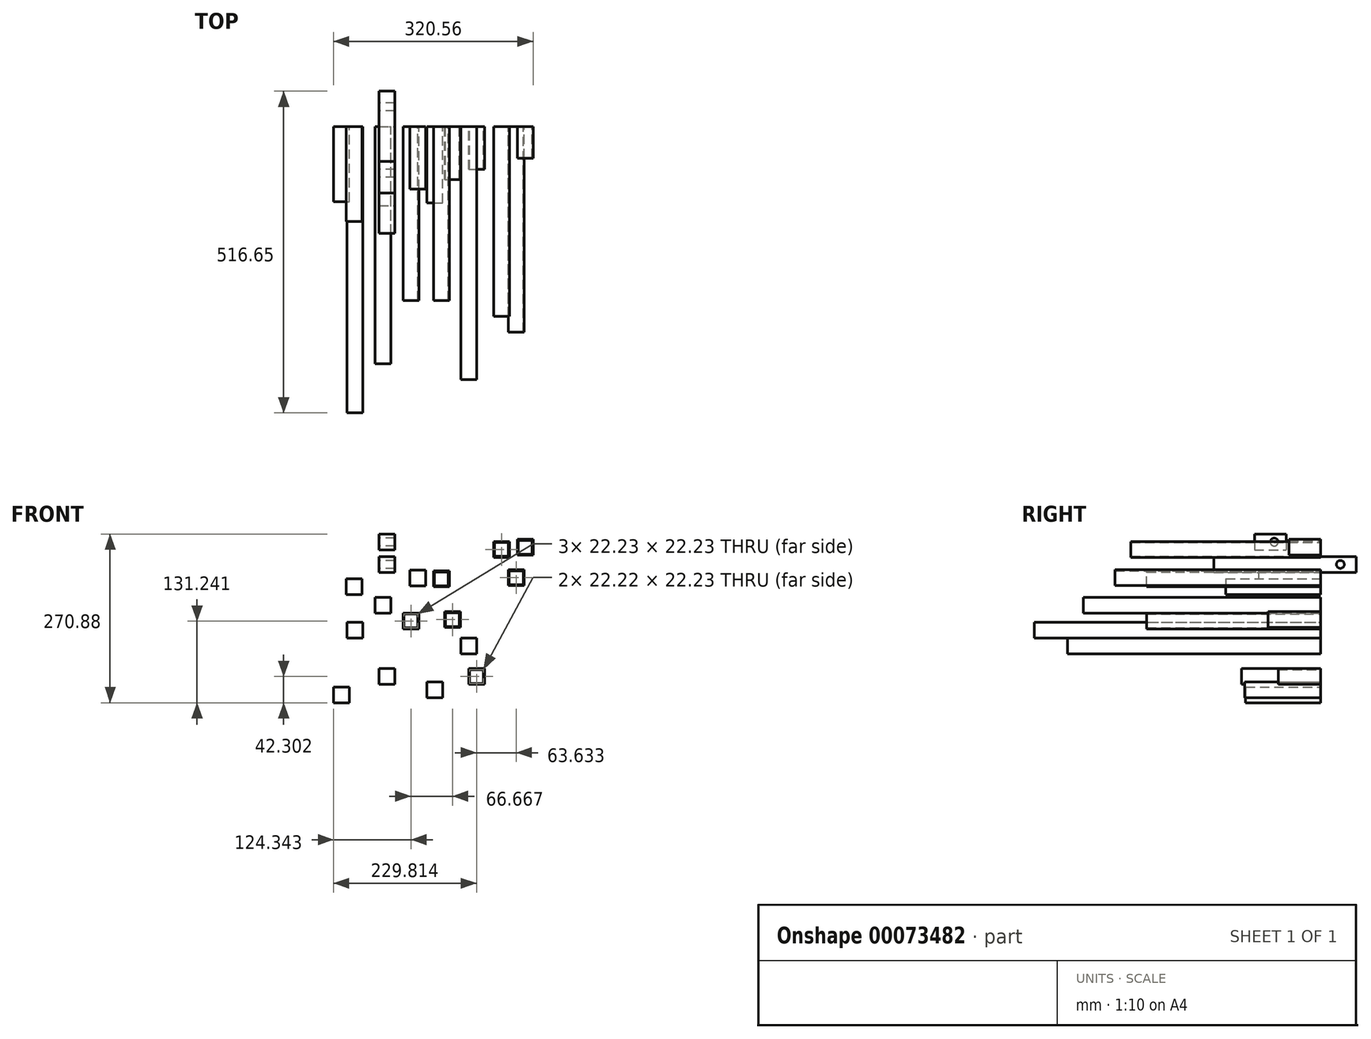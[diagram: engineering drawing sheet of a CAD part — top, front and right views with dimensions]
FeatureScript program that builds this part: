
annotation { "Feature Type Name" : "Feature", "Feature Type Description" : "" }
export const myFeature = defineFeature(function(context is Context, id is Id, definition is map)
    precondition{}
    {
        {
            var Q0;
            Q0=qCreatedBy(makeId("Front.planeOp"),FACE);
            var sketch = newSketch(context, id + "F0", { "sketchPlane" : qUnion([Q0])});
            skLineSegment(sketch, "E0.bottom", {"start": v(-6.69, -14.03) * mm, "end": v(18.71, -14.03) * mm});
            skLineSegment(sketch, "E0.top", {"start": v(-6.69, 11.37) * mm, "end": v(18.71, 11.37) * mm});
            skLineSegment(sketch, "E0.left", {"start": v(-6.69, -14.03) * mm, "end": v(-6.69, 11.37) * mm});
            skLineSegment(sketch, "E0.right", {"start": v(18.71, -14.03) * mm, "end": v(18.71, 11.37) * mm});
            skSolve(sketch);
        }
        {
            var Q0;
            Q0=makeQuery(id+"F0.imprint","IMPRINT",FACE,{"disambiguationData":[TD([[makeQuery(id+"F0.imprint","IMPRINT",EDGE,{"derivedFrom":sQuery(id+"F0.wireOp",EDGE,"E0.bottom")}),1.0]])]});
            extrude(context, id + "F1", {"entities" : qUnion([Q0]), "depth" : 381 * mm});
        }
        {
            var Q0;
            Q0=qCreatedBy(makeId("Front.planeOp"),FACE);
            var sketch = newSketch(context, id + "F2", { "sketchPlane" : qUnion([Q0])});
            skLineSegment(sketch, "E1.bottom", {"start": v(38.41, -39.74) * mm, "end": v(63.81, -39.74) * mm});
            skLineSegment(sketch, "E1.top", {"start": v(38.41, -14.34) * mm, "end": v(63.81, -14.34) * mm});
            skLineSegment(sketch, "E1.left", {"start": v(38.41, -39.74) * mm, "end": v(38.41, -14.34) * mm});
            skLineSegment(sketch, "E1.right", {"start": v(63.81, -39.74) * mm, "end": v(63.81, -14.34) * mm});
            skLineSegment(sketch, "E2.0", {"start": v(62.23, -38.15) * mm, "end": v(62.23, -15.93) * mm});
            skLineSegment(sketch, "E2.1", {"start": v(40, -38.15) * mm, "end": v(62.23, -38.15) * mm});
            skLineSegment(sketch, "E2.2", {"start": v(40, -38.15) * mm, "end": v(40, -15.93) * mm});
            skLineSegment(sketch, "E2.3", {"start": v(40, -15.93) * mm, "end": v(62.23, -15.93) * mm});
            skSolve(sketch);
        }
        {
            var Q0;
            Q0=makeQuery(id+"F2.imprint","IMPRINT",FACE,{"disambiguationData":[TD([[makeQuery(id+"F2.imprint","IMPRINT",EDGE,{"derivedFrom":sQuery(id+"F2.wireOp",EDGE,"E1.bottom")}),1.0]])]});
            extrude(context, id + "F3", {"entities" : qUnion([Q0]), "depth" : 279.4 * mm});
        }
        {
            var Q0;
            Q0=qCreatedBy(makeId("Front.planeOp"),FACE);
            var sketch = newSketch(context, id + "F4", { "sketchPlane" : qUnion([Q0])});
            skLineSegment(sketch, "E3.bottom", {"start": v(-52.82, 41.02) * mm, "end": v(-27.42, 41.02) * mm});
            skLineSegment(sketch, "E3.top", {"start": v(-52.82, 15.62) * mm, "end": v(-27.42, 15.62) * mm});
            skLineSegment(sketch, "E3.left", {"start": v(-52.82, 41.02) * mm, "end": v(-52.82, 15.62) * mm});
            skLineSegment(sketch, "E3.right", {"start": v(-27.42, 41.02) * mm, "end": v(-27.42, 15.62) * mm});
            skSolve(sketch);
        }
        {
            var Q0;
            Q0=makeQuery(id+"F4.imprint","IMPRINT",FACE,{"disambiguationData":[TD([[makeQuery(id+"F4.imprint","IMPRINT",EDGE,{"derivedFrom":sQuery(id+"F4.wireOp",EDGE,"E3.bottom")}),-1.0]])]});
            extrude(context, id + "F5", {"entities" : qUnion([Q0]), "depth" : 152.4 * mm});
        }
        {
            var Q0;
            Q0=qCreatedBy(makeId("Right.planeOp"),FACE);
            var sketch = newSketch(context, id + "F6", { "sketchPlane" : qUnion([Q0])});
            skLineSegment(sketch, "E4.bottom", {"start": v(-171.69, 76.74) * mm, "end": v(56.91, 76.74) * mm});
            skLineSegment(sketch, "E4.top", {"start": v(-171.69, 51.34) * mm, "end": v(56.91, 51.34) * mm});
            skLineSegment(sketch, "E4.left", {"start": v(-171.69, 76.74) * mm, "end": v(-171.69, 51.34) * mm});
            skLineSegment(sketch, "E4.right", {"start": v(56.91, 76.74) * mm, "end": v(56.91, 51.34) * mm});
            skCircle(sketch, "E5", {"center": v(31.51, 64.04) * mm, "radius": 6.35 * mm});
            skPoint(sketch, "E5.centerSnap0", {"position": v(56.91, 64.04) * mm});
            skSolve(sketch);
        }
        {
            var Q0;
            Q0=makeQuery(id+"F6.imprint","IMPRINT",FACE,{"disambiguationData":[TD([[makeQuery(id+"F6.imprint","IMPRINT",EDGE,{"derivedFrom":sQuery(id+"F6.wireOp",EDGE,"E4.bottom")}),-1.0]])]});
            extrude(context, id + "F7", {"entities" : qUnion([Q0]), "depth" : 25.4 * mm});
        }
        {
            var Q0;
            Q0=qCreatedBy(makeId("Right.planeOp"),FACE);
            var sketch = newSketch(context, id + "F8", { "sketchPlane" : qUnion([Q0])});
            skLineSegment(sketch, "E6.bottom", {"start": v(-106.42, 112.6) * mm, "end": v(-55.62, 112.6) * mm});
            skLineSegment(sketch, "E6.top", {"start": v(-106.42, 87.2) * mm, "end": v(-55.62, 87.2) * mm});
            skLineSegment(sketch, "E6.left", {"start": v(-106.42, 112.6) * mm, "end": v(-106.42, 87.2) * mm});
            skLineSegment(sketch, "E6.right", {"start": v(-55.62, 112.6) * mm, "end": v(-55.62, 87.2) * mm});
            skCircle(sketch, "E7", {"center": v(-74.67, 99.9) * mm, "radius": 6.35 * mm});
            skPoint(sketch, "E7.centerSnap0", {"position": v(-55.62, 99.9) * mm});
            skSolve(sketch);
        }
        {
            var Q0;
            Q0=makeQuery(id+"F8.imprint","IMPRINT",FACE,{"disambiguationData":[TD([[makeQuery(id+"F8.imprint","IMPRINT",EDGE,{"derivedFrom":sQuery(id+"F8.wireOp",EDGE,"E6.bottom")}),-1.0]])]});
            extrude(context, id + "F9", {"entities" : qUnion([Q0]), "depth" : 25.4 * mm});
        }
        {
            var Q0;
            Q0=qCreatedBy(makeId("Front.planeOp"),FACE);
            var sketch = newSketch(context, id + "F10", { "sketchPlane" : qUnion([Q0])});
            skLineSegment(sketch, "E8.bottom", {"start": v(-51.42, -54.05) * mm, "end": v(-26.02, -54.05) * mm});
            skLineSegment(sketch, "E8.top", {"start": v(-51.42, -28.65) * mm, "end": v(-26.02, -28.65) * mm});
            skLineSegment(sketch, "E8.left", {"start": v(-51.42, -54.05) * mm, "end": v(-51.42, -28.65) * mm});
            skLineSegment(sketch, "E8.right", {"start": v(-26.02, -54.05) * mm, "end": v(-26.02, -28.65) * mm});
            skSolve(sketch);
        }
        {
            var Q0;
            Q0=makeQuery(id+"F10.imprint","IMPRINT",FACE,{"disambiguationData":[TD([[makeQuery(id+"F10.imprint","IMPRINT",EDGE,{"derivedFrom":sQuery(id+"F10.wireOp",EDGE,"E8.bottom")}),1.0]])]});
            extrude(context, id + "F11", {"entities" : qUnion([Q0]), "depth" : 459.74 * mm});
        }
        {
            var Q0;
            Q0=qCreatedBy(makeId("Front.planeOp"),FACE);
            var sketch = newSketch(context, id + "F12", { "sketchPlane" : qUnion([Q0])});
            skLineSegment(sketch, "E9.bottom", {"start": v(49.68, 54.58) * mm, "end": v(75.08, 54.58) * mm});
            skLineSegment(sketch, "E9.top", {"start": v(49.68, 29.18) * mm, "end": v(75.08, 29.18) * mm});
            skLineSegment(sketch, "E9.left", {"start": v(49.68, 54.58) * mm, "end": v(49.68, 29.18) * mm});
            skLineSegment(sketch, "E9.right", {"start": v(75.08, 54.58) * mm, "end": v(75.08, 29.18) * mm});
            skSolve(sketch);
        }
        {
            var Q0;
            Q0=makeQuery(id+"F12.imprint","IMPRINT",FACE,{"disambiguationData":[TD([[makeQuery(id+"F12.imprint","IMPRINT",EDGE,{"derivedFrom":sQuery(id+"F12.wireOp",EDGE,"E9.bottom")}),-1.0]])]});
            extrude(context, id + "F13", {"entities" : qUnion([Q0]), "depth" : 100.08 * mm});
        }
        {
            var Q0;
            Q0=qCreatedBy(makeId("Front.planeOp"),FACE);
            var sketch = newSketch(context, id + "F14", { "sketchPlane" : qUnion([Q0])});
            skLineSegment(sketch, "E10.bottom", {"start": v(76.44, -124.58) * mm, "end": v(101.84, -124.58) * mm});
            skLineSegment(sketch, "E10.top", {"start": v(76.44, -149.98) * mm, "end": v(101.84, -149.98) * mm});
            skLineSegment(sketch, "E10.left", {"start": v(76.44, -124.58) * mm, "end": v(76.44, -149.98) * mm});
            skLineSegment(sketch, "E10.right", {"start": v(101.84, -124.58) * mm, "end": v(101.84, -149.98) * mm});
            skSolve(sketch);
        }
        {
            var Q0;
            Q0=makeQuery(id+"F14.imprint","IMPRINT",FACE,{"disambiguationData":[TD([[makeQuery(id+"F14.imprint","IMPRINT",EDGE,{"derivedFrom":sQuery(id+"F14.wireOp",EDGE,"E10.bottom")}),-1.0]])]});
            extrude(context, id + "F15", {"entities" : qUnion([Q0]), "depth" : 122.33 * mm});
        }
        {
            var Q0;
            Q0=qCreatedBy(makeId("Front.planeOp"),FACE);
            var sketch = newSketch(context, id + "F16", { "sketchPlane" : qUnion([Q0])});
            skLineSegment(sketch, "E11.bottom", {"start": v(-73.23, -132.88) * mm, "end": v(-47.83, -132.88) * mm});
            skLineSegment(sketch, "E11.top", {"start": v(-73.23, -158.28) * mm, "end": v(-47.83, -158.28) * mm});
            skLineSegment(sketch, "E11.left", {"start": v(-73.23, -132.88) * mm, "end": v(-73.23, -158.28) * mm});
            skLineSegment(sketch, "E11.right", {"start": v(-47.83, -132.88) * mm, "end": v(-47.83, -158.28) * mm});
            skSolve(sketch);
        }
        {
            var Q0;
            Q0=makeQuery(id+"F16.imprint","IMPRINT",FACE,{"disambiguationData":[TD([[makeQuery(id+"F16.imprint","IMPRINT",EDGE,{"derivedFrom":sQuery(id+"F16.wireOp",EDGE,"E11.bottom")}),-1.0]])]});
            extrude(context, id + "F17", {"entities" : qUnion([Q0]), "depth" : 120.6 * mm});
        }
        {
            var Q0;
            Q0=qCreatedBy(makeId("Front.planeOp"),FACE);
            var sketch = newSketch(context, id + "F18", { "sketchPlane" : qUnion([Q0])});
            skLineSegment(sketch, "E12.bottom", {"start": v(0, -103.28) * mm, "end": v(25.4, -103.28) * mm});
            skLineSegment(sketch, "E12.top", {"start": v(0, -128.68) * mm, "end": v(25.4, -128.68) * mm});
            skLineSegment(sketch, "E12.left", {"start": v(0, -103.28) * mm, "end": v(0, -128.68) * mm});
            skLineSegment(sketch, "E12.right", {"start": v(25.4, -103.28) * mm, "end": v(25.4, -128.68) * mm});
            skSolve(sketch);
        }
        {
            var Q0;
            Q0=makeQuery(id+"F18.imprint","IMPRINT",FACE,{"disambiguationData":[TD([[makeQuery(id+"F18.imprint","IMPRINT",EDGE,{"derivedFrom":sQuery(id+"F18.wireOp",EDGE,"E12.bottom")}),-1.0]])]});
            extrude(context, id + "F19", {"entities" : qUnion([Q0]), "depth" : 127 * mm});
        }
        {
            var Q0;
            Q0=qCreatedBy(makeId("Front.planeOp"),FACE);
            var sketch = newSketch(context, id + "F20", { "sketchPlane" : qUnion([Q0])});
            skLineSegment(sketch, "E13.bottom", {"start": v(131.36, -54.53) * mm, "end": v(156.76, -54.53) * mm});
            skLineSegment(sketch, "E13.top", {"start": v(131.36, -79.93) * mm, "end": v(156.76, -79.93) * mm});
            skLineSegment(sketch, "E13.left", {"start": v(131.36, -54.53) * mm, "end": v(131.36, -79.93) * mm});
            skLineSegment(sketch, "E13.right", {"start": v(156.76, -54.53) * mm, "end": v(156.76, -79.93) * mm});
            skSolve(sketch);
        }
        {
            var Q0;
            Q0=makeQuery(id+"F20.imprint","IMPRINT",FACE,{"disambiguationData":[TD([[makeQuery(id+"F20.imprint","IMPRINT",EDGE,{"derivedFrom":sQuery(id+"F20.wireOp",EDGE,"E13.bottom")}),-1.0]])]});
            extrude(context, id + "F21", {"entities" : qUnion([Q0]), "depth" : 406.4 * mm});
        }
        {
            var Q0;
            Q0=qCreatedBy(makeId("Front.planeOp"),FACE);
            var sketch = newSketch(context, id + "F22", { "sketchPlane" : qUnion([Q0])});
            skLineSegment(sketch, "E14.rect.bottom", {"start": v(111.05, 29.62) * mm, "end": v(88.82, 29.62) * mm});
            skLineSegment(sketch, "E14.rect.top", {"start": v(111.05, 51.84) * mm, "end": v(88.82, 51.84) * mm});
            skLineSegment(sketch, "E14.rect.left", {"start": v(111.05, 29.62) * mm, "end": v(111.05, 51.84) * mm});
            skLineSegment(sketch, "E14.rect.right", {"start": v(88.82, 29.62) * mm, "end": v(88.82, 51.84) * mm});
            skPoint(sketch, "E14.rect.middle", {"position": v(99.93, 40.73) * mm});
            skLineSegment(sketch, "E15.0", {"start": v(112.63, 53.43) * mm, "end": v(87.23, 53.43) * mm});
            skLineSegment(sketch, "E15.1", {"start": v(112.63, 28.03) * mm, "end": v(112.63, 53.43) * mm});
            skLineSegment(sketch, "E15.2", {"start": v(112.63, 28.03) * mm, "end": v(87.23, 28.03) * mm});
            skLineSegment(sketch, "E15.3", {"start": v(87.23, 28.03) * mm, "end": v(87.23, 53.43) * mm});
            skSolve(sketch);
        }
        {
            var Q0;
            Q0=qSketchRegion(id+"F22",true);
            extrude(context, id + "F23", {"entities" : qUnion([Q0]), "depth" : 279.4 * mm});
        }
        {
            var Q0;
            Q0=qCreatedBy(makeId("Front.planeOp"),FACE);
            var sketch = newSketch(context, id + "F24", { "sketchPlane" : qUnion([Q0])});
            skLineSegment(sketch, "E16.bottom", {"start": v(183.84, 75.25) * mm, "end": v(209.24, 75.25) * mm});
            skLineSegment(sketch, "E16.top", {"start": v(183.84, 100.65) * mm, "end": v(209.24, 100.65) * mm});
            skLineSegment(sketch, "E16.left", {"start": v(183.84, 75.25) * mm, "end": v(183.84, 100.65) * mm});
            skLineSegment(sketch, "E16.right", {"start": v(209.24, 75.25) * mm, "end": v(209.24, 100.65) * mm});
            skLineSegment(sketch, "E17.bottom", {"start": v(185.43, 99.07) * mm, "end": v(207.66, 99.07) * mm});
            skLineSegment(sketch, "E17.top", {"start": v(185.43, 76.84) * mm, "end": v(207.66, 76.84) * mm});
            skLineSegment(sketch, "E17.left", {"start": v(185.43, 99.07) * mm, "end": v(185.43, 76.84) * mm});
            skLineSegment(sketch, "E17.right", {"start": v(207.66, 99.07) * mm, "end": v(207.66, 76.84) * mm});
            skSolve(sketch);
        }
        {
            var Q0;
            Q0=makeQuery(id+"F24.imprint","IMPRINT",FACE,{"disambiguationData":[TD([[makeQuery(id+"F24.imprint","IMPRINT",EDGE,{"derivedFrom":sQuery(id+"F24.wireOp",EDGE,"E16.bottom")}),1.0]])]});
            extrude(context, id + "F25", {"entities" : qUnion([Q0]), "depth" : 304.8 * mm});
        }
        {
            var Q0;
            Q0=qCreatedBy(makeId("Front.planeOp"),FACE);
            var sketch = newSketch(context, id + "F26", { "sketchPlane" : qUnion([Q0])});
            skLineSegment(sketch, "E18.bottom", {"start": v(221.93, 104.17) * mm, "end": v(247.33, 104.17) * mm});
            skLineSegment(sketch, "E18.top", {"start": v(221.93, 78.77) * mm, "end": v(247.33, 78.77) * mm});
            skLineSegment(sketch, "E18.left", {"start": v(221.93, 104.17) * mm, "end": v(221.93, 78.77) * mm});
            skLineSegment(sketch, "E18.right", {"start": v(247.33, 104.17) * mm, "end": v(247.33, 78.77) * mm});
            skLineSegment(sketch, "E19.bottom", {"start": v(223.52, 80.36) * mm, "end": v(245.74, 80.36) * mm});
            skLineSegment(sketch, "E19.top", {"start": v(223.52, 102.58) * mm, "end": v(245.74, 102.58) * mm});
            skLineSegment(sketch, "E19.left", {"start": v(223.52, 80.36) * mm, "end": v(223.52, 102.58) * mm});
            skLineSegment(sketch, "E19.right", {"start": v(245.74, 80.36) * mm, "end": v(245.74, 102.58) * mm});
            skSolve(sketch);
        }
        {
            var Q0;
            Q0=makeQuery(id+"F26.imprint","IMPRINT",FACE,{"disambiguationData":[TD([[makeQuery(id+"F26.imprint","IMPRINT",EDGE,{"derivedFrom":sQuery(id+"F26.wireOp",EDGE,"E18.bottom")}),-1.0]])]});
            extrude(context, id + "F27", {"entities" : qUnion([Q0]), "depth" : 50.8 * mm});
        }
        {
            var Q0;
            Q0=qCreatedBy(makeId("Front.planeOp"),FACE);
            var sketch = newSketch(context, id + "F28", { "sketchPlane" : qUnion([Q0])});
            skLineSegment(sketch, "E20.bottom", {"start": v(207.52, 55.28) * mm, "end": v(232.92, 55.28) * mm});
            skLineSegment(sketch, "E20.top", {"start": v(207.52, 29.88) * mm, "end": v(232.92, 29.88) * mm});
            skLineSegment(sketch, "E20.left", {"start": v(207.52, 55.28) * mm, "end": v(207.52, 29.88) * mm});
            skLineSegment(sketch, "E20.right", {"start": v(232.92, 55.28) * mm, "end": v(232.92, 29.88) * mm});
            skLineSegment(sketch, "E21.0", {"start": v(231.33, 53.7) * mm, "end": v(231.33, 31.47) * mm});
            skLineSegment(sketch, "E21.1", {"start": v(209.1, 53.7) * mm, "end": v(231.33, 53.7) * mm});
            skLineSegment(sketch, "E21.2", {"start": v(209.1, 53.7) * mm, "end": v(209.1, 31.47) * mm});
            skLineSegment(sketch, "E21.3", {"start": v(209.1, 31.47) * mm, "end": v(231.33, 31.47) * mm});
            skSolve(sketch);
        }
        {
            var Q0;
            Q0=makeQuery(id+"F28.imprint","IMPRINT",FACE,{"disambiguationData":[TD([[makeQuery(id+"F28.imprint","IMPRINT",EDGE,{"derivedFrom":sQuery(id+"F28.wireOp",EDGE,"E20.bottom")}),-1.0]])]});
            extrude(context, id + "F29", {"entities" : qUnion([Q0]), "depth" : 330.2 * mm});
        }
        {
            var Q0;
            Q0=qCreatedBy(makeId("Front.planeOp"),FACE);
            var sketch = newSketch(context, id + "F30", { "sketchPlane" : qUnion([Q0])});
            skLineSegment(sketch, "E22.bottom", {"start": v(105.08, -37.45) * mm, "end": v(130.48, -37.45) * mm});
            skLineSegment(sketch, "E22.top", {"start": v(105.08, -12.05) * mm, "end": v(130.48, -12.05) * mm});
            skLineSegment(sketch, "E22.left", {"start": v(105.08, -37.45) * mm, "end": v(105.08, -12.05) * mm});
            skLineSegment(sketch, "E22.right", {"start": v(130.48, -37.45) * mm, "end": v(130.48, -12.05) * mm});
            skLineSegment(sketch, "E23.0", {"start": v(128.9, -35.86) * mm, "end": v(128.9, -13.64) * mm});
            skLineSegment(sketch, "E23.1", {"start": v(106.67, -35.86) * mm, "end": v(128.9, -35.86) * mm});
            skLineSegment(sketch, "E23.2", {"start": v(106.67, -35.86) * mm, "end": v(106.67, -13.64) * mm});
            skLineSegment(sketch, "E23.3", {"start": v(106.67, -13.64) * mm, "end": v(128.9, -13.64) * mm});
            skSolve(sketch);
        }
        {
            var Q0;
            Q0=makeQuery(id+"F30.imprint","IMPRINT",FACE,{"disambiguationData":[TD([[makeQuery(id+"F30.imprint","IMPRINT",EDGE,{"derivedFrom":sQuery(id+"F30.wireOp",EDGE,"E22.bottom")}),1.0]])]});
            extrude(context, id + "F31", {"entities" : qUnion([Q0]), "depth" : 84.84 * mm});
        }
        {
            var Q0;
            Q0=qCreatedBy(makeId("Front.planeOp"),FACE);
            var sketch = newSketch(context, id + "F32", { "sketchPlane" : qUnion([Q0])});
            skLineSegment(sketch, "E24.bottom", {"start": v(143.88, -128.68) * mm, "end": v(169.28, -128.68) * mm});
            skLineSegment(sketch, "E24.top", {"start": v(143.88, -103.28) * mm, "end": v(169.28, -103.28) * mm});
            skLineSegment(sketch, "E24.left", {"start": v(143.88, -128.68) * mm, "end": v(143.88, -103.28) * mm});
            skLineSegment(sketch, "E24.right", {"start": v(169.28, -128.68) * mm, "end": v(169.28, -103.28) * mm});
            skLineSegment(sketch, "E25.0", {"start": v(167.7, -127.1) * mm, "end": v(167.7, -104.87) * mm});
            skLineSegment(sketch, "E25.1", {"start": v(145.47, -127.1) * mm, "end": v(167.7, -127.1) * mm});
            skLineSegment(sketch, "E25.2", {"start": v(145.47, -127.1) * mm, "end": v(145.47, -104.87) * mm});
            skLineSegment(sketch, "E25.3", {"start": v(145.47, -104.87) * mm, "end": v(167.7, -104.87) * mm});
            skSolve(sketch);
        }
        {
            var Q0;
            Q0=makeQuery(id+"F32.imprint","IMPRINT",FACE,{"disambiguationData":[TD([[makeQuery(id+"F32.imprint","IMPRINT",EDGE,{"derivedFrom":sQuery(id+"F32.wireOp",EDGE,"E24.bottom")}),1.0]])]});
            extrude(context, id + "F33", {"entities" : qUnion([Q0]), "depth" : 68.26 * mm});
        }
    });
